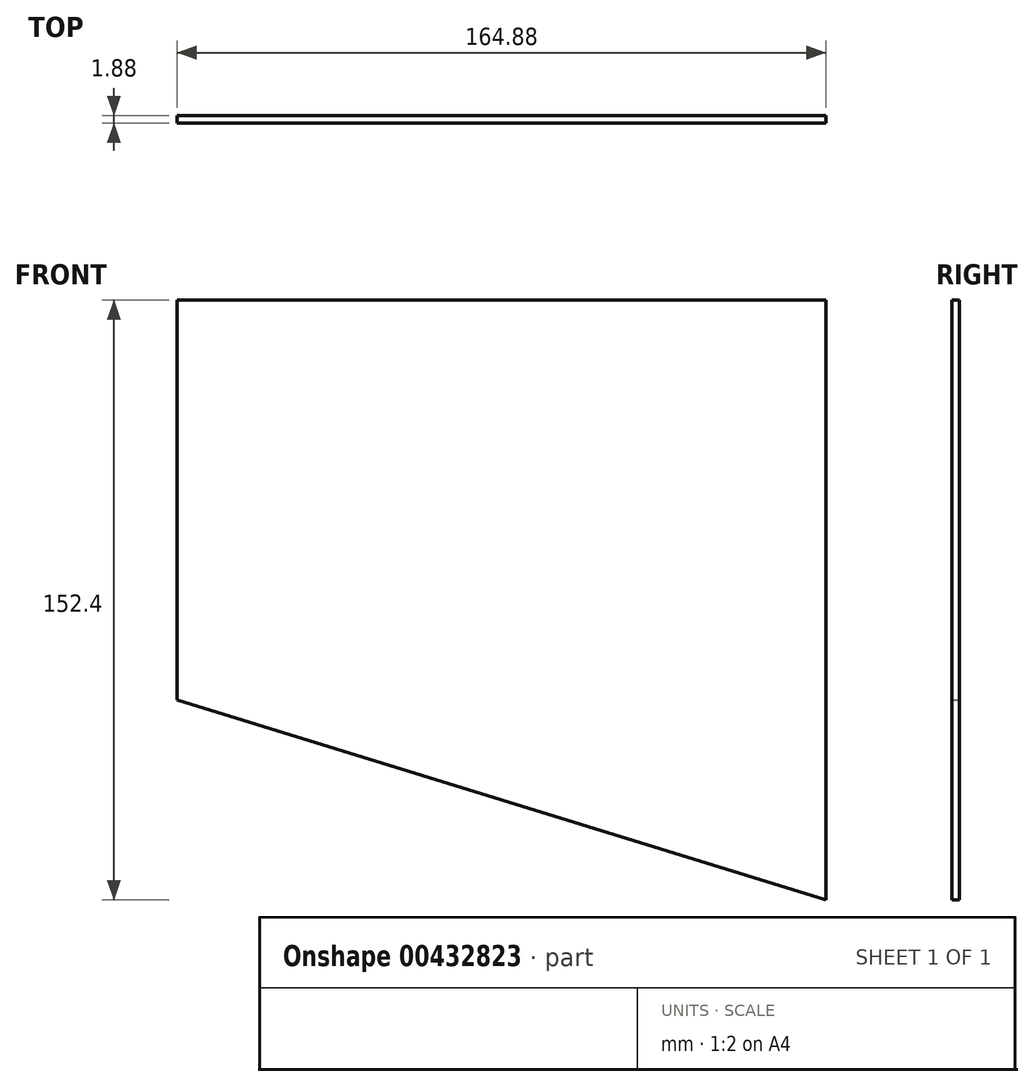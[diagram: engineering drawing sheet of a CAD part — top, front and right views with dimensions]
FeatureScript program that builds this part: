
annotation { "Feature Type Name" : "Feature", "Feature Type Description" : "" }
export const myFeature = defineFeature(function(context is Context, id is Id, definition is map)
    precondition{}
    {
        {
            var Q0;
            Q0=qCreatedBy(makeId("Front.planeOp"),FACE);
            var sketch = newSketch(context, id + "F0", { "sketchPlane" : qUnion([Q0])});
            skLineSegment(sketch, "E0", {"start": v(0, 0) * mm, "end": v(0, 152.4) * mm});
            skLineSegment(sketch, "E1", {"start": v(0, 152.4) * mm, "end": v(-164.88, 152.4) * mm});
            skLineSegment(sketch, "E2", {"start": v(-164.88, 152.4) * mm, "end": v(-164.88, 50.8) * mm});
            skLineSegment(sketch, "E3", {"start": v(-164.88, 50.8) * mm, "end": v(0, 0) * mm});
            skSolve(sketch);
        }
        {
            var Q0;
            Q0 = qSketchRegion(id + "F0", true);
            extrude(context, id + "F1", {"entities" : qUnion([Q0]), "depth" : 1.88 * mm});
        }
    });
